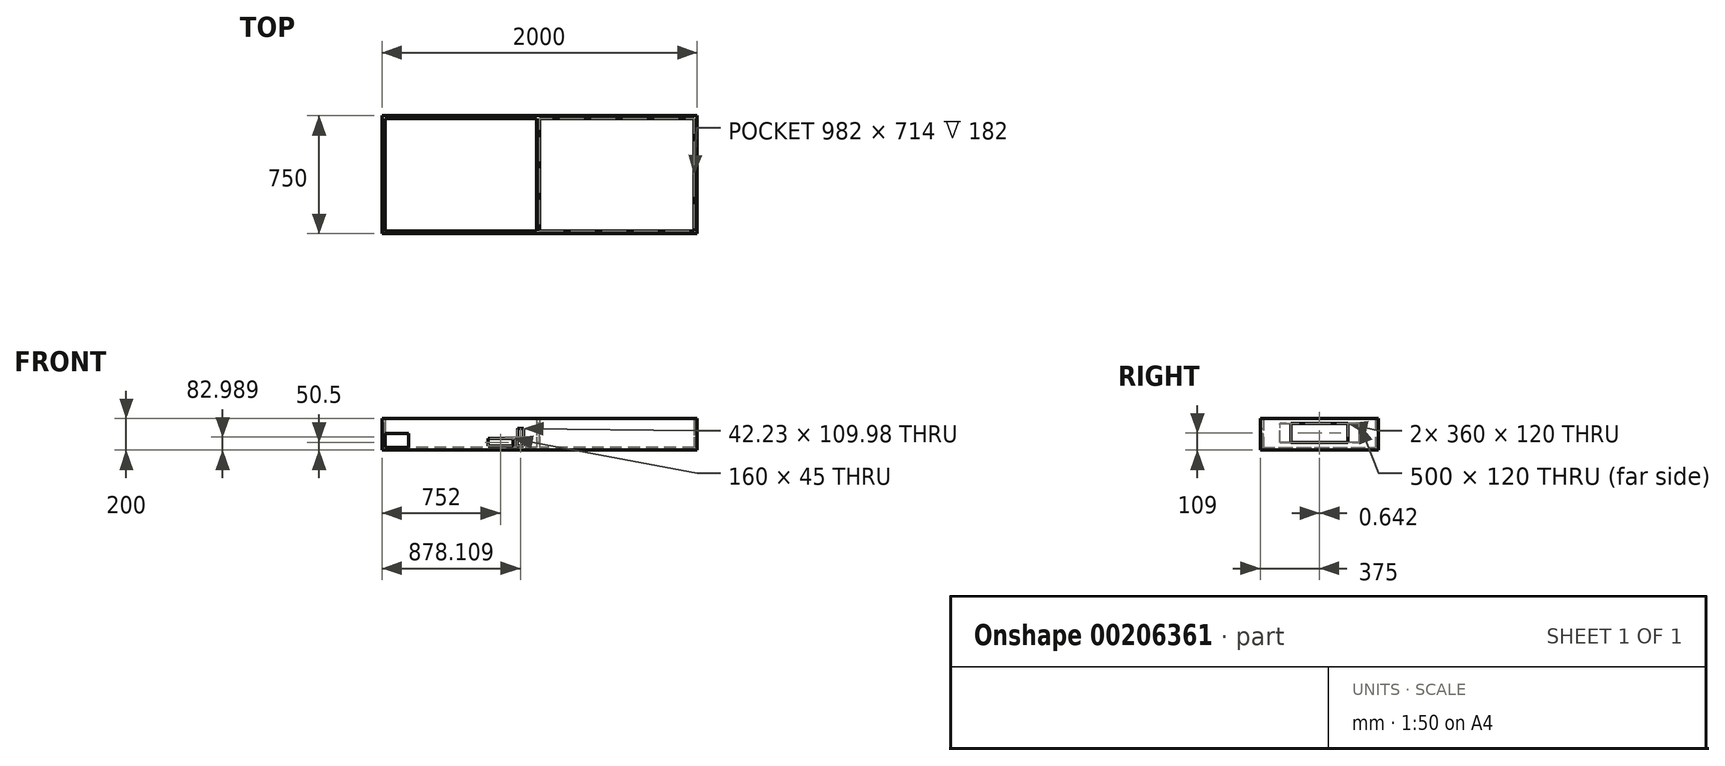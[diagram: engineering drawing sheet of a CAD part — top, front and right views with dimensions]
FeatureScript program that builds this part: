
annotation { "Feature Type Name" : "Feature", "Feature Type Description" : "" }
export const myFeature = defineFeature(function(context is Context, id is Id, definition is map)
    precondition{}
    {
        {
            var Q0;
            Q0=qCreatedBy(makeId("Top.planeOp"),FACE);
            var sketch = newSketch(context, id + "F0", { "sketchPlane" : qUnion([Q0])});
            skLineSegment(sketch, "E0.bottom", {"start": v(1000, -375) * mm, "end": v(-1000, -375) * mm});
            skLineSegment(sketch, "E0.top", {"start": v(1000, 375) * mm, "end": v(-1000, 375) * mm});
            skLineSegment(sketch, "E0.left", {"start": v(1000, -375) * mm, "end": v(1000, 375) * mm});
            skLineSegment(sketch, "E0.right", {"start": v(-1000, -375) * mm, "end": v(-1000, 375) * mm});
            skPoint(sketch, "E0.middle", {"position": v(0, 0) * mm});
            skSolve(sketch);
        }
        {
            var Q0;
            Q0=makeQuery(id+"F0.imprint","IMPRINT",FACE,{"disambiguationData":[TD([[makeQuery(id+"F0.imprint","IMPRINT",EDGE,{"derivedFrom":sQuery(id+"F0.wireOp",EDGE,"E0.bottom")}),-1.0]])]});
            extrude(context, id + "F1", {"entities" : qUnion([Q0]), "depth" : 200 * mm});
        }
        {
            var Q0;
            Q0=makeQuery(id+"F1.opExtrude","CAP_FACE",FACE,{"disambiguationData":[OSD([sQuery(id+"F0.wireOp",EDGE,"E0.bottom"),sQuery(id+"F0.wireOp",EDGE,"E0.top"),sQuery(id+"F0.wireOp",EDGE,"E0.left"),sQuery(id+"F0.wireOp",EDGE,"E0.right")])],"isStart":false});
            shell(context, id + "F2", {"entities" : qUnion([Q0]), "thickness" : 18 * mm});
        }
        {
            var Q0;
            Q0=makeQuery(id+"F2.opShell","OFFSET_FACE",FACE,{"disambiguationData":[OSD([sQuery(id+"F0.wireOp",EDGE,"E0.bottom"),sQuery(id+"F0.wireOp",EDGE,"E0.top"),sQuery(id+"F0.wireOp",EDGE,"E0.left"),sQuery(id+"F0.wireOp",EDGE,"E0.right")])]});
            var sketch = newSketch(context, id + "F3", { "sketchPlane" : qUnion([Q0])});
            skLineSegment(sketch, "E1.bottom", {"start": v(0, 357) * mm, "end": v(-18, 357) * mm});
            skLineSegment(sketch, "E1.top", {"start": v(0, -357) * mm, "end": v(-18, -357) * mm});
            skLineSegment(sketch, "E1.left", {"start": v(0, 357) * mm, "end": v(0, -357) * mm});
            skLineSegment(sketch, "E1.right", {"start": v(-18, 357) * mm, "end": v(-18, -357) * mm});
            skSolve(sketch);
        }
        {
            var Q0;
            Q0=makeQuery(id+"F3.imprint","IMPRINT",FACE,{"disambiguationData":[TD([[makeQuery(id+"F3.imprint","IMPRINT",EDGE,{"derivedFrom":sQuery(id+"F3.wireOp",EDGE,"E1.bottom")}),1.0]])]});
            extrude(context, id + "F4", {"entities" : qUnion([Q0]), "operationType" : NewBodyOperationType.ADD, "depth" : 182 * mm});
        }
        {
            var Q0;
            Q0=makeQuery(id+"F4.opExtrude","SWEPT_FACE",FACE,{"disambiguationData":[OSD([sQuery(id+"F3.wireOp",EDGE,"E1.right")])]});
            var sketch = newSketch(context, id + "F5", { "sketchPlane" : qUnion([Q0])});
            skLineSegment(sketch, "E2", {"start": v(0, 200) * mm, "end": v(0, 169) * mm});
            skLineSegment(sketch, "E3", {"start": v(0, 169) * mm, "end": v(250, 169) * mm});
            skLineSegment(sketch, "E4", {"start": v(250, 169) * mm, "end": v(250, 49) * mm});
            skLineSegment(sketch, "E5", {"start": v(250, 49) * mm, "end": v(-250, 49) * mm});
            skLineSegment(sketch, "E6", {"start": v(-250, 49) * mm, "end": v(-250, 169) * mm});
            skLineSegment(sketch, "E7", {"start": v(-250, 169) * mm, "end": v(0, 169) * mm});
            skSolve(sketch);
        }
        {
            var Q0;
            Q0=makeQuery(id+"F5.imprint","IMPRINT",FACE,{"disambiguationData":[TD([[makeQuery(id+"F5.imprint","IMPRINT",EDGE,{"derivedFrom":sQuery(id+"F5.wireOp",EDGE,"E3")}),-1.0]])]});
            extrude(context, id + "F6", {"entities" : qUnion([Q0]), "operationType" : NewBodyOperationType.REMOVE, "oppositeDirection" : true, "depth" : 25 * mm});
        }
        {
            var Q0;
            {var subQ1=sQuery(id+"F0.wireOp",EDGE,"E0.right");var subQ4=sQuery(id+"F0.wireOp",EDGE,"E0.bottom");Q0=makeQuery(id+"F4.boolean.opBoolean","SPLIT",FACE,{"disambiguationData":[TD([makeQuery(id+"F2.opShell","OFFSET_FACE",FACE,{"disambiguationData":[OSD([subQ1])]})])],"derivedFrom":makeQuery(id+"F2.opShell","OFFSET_FACE",FACE,{"disambiguationData":[OSD([subQ4])]})});}
            var sketch = newSketch(context, id + "F7", { "sketchPlane" : qUnion([Q0])});
            skLineSegment(sketch, "E8.bottom", {"start": v(982, 18) * mm, "end": v(832, 18) * mm});
            skLineSegment(sketch, "E8.top", {"start": v(982, 106.6) * mm, "end": v(832, 106.6) * mm});
            skLineSegment(sketch, "E8.left", {"start": v(982, 18) * mm, "end": v(982, 106.6) * mm});
            skLineSegment(sketch, "E8.right", {"start": v(832, 18) * mm, "end": v(832, 106.6) * mm});
            skLineSegment(sketch, "E9", {"start": v(18, 18) * mm, "end": v(93.34, 18) * mm});
            skLineSegment(sketch, "E10", {"start": v(328, 18) * mm, "end": v(328, 28) * mm});
            skLineSegment(sketch, "E11", {"start": v(328, 28) * mm, "end": v(168, 28) * mm});
            skLineSegment(sketch, "E12", {"start": v(168, 28) * mm, "end": v(168, 18) * mm});
            skLineSegment(sketch, "E13", {"start": v(168, 28) * mm, "end": v(143, 28) * mm});
            skLineSegment(sketch, "E14", {"start": v(143, 28) * mm, "end": v(103, 28) * mm});
            skLineSegment(sketch, "E15", {"start": v(103, 28) * mm, "end": v(18, 28) * mm});
            skLineSegment(sketch, "E16", {"start": v(103, 28) * mm, "end": v(100.78, 137.98) * mm});
            skLineSegment(sketch, "E17", {"start": v(100.78, 137.98) * mm, "end": v(140.78, 137.98) * mm});
            skLineSegment(sketch, "E18", {"start": v(140.78, 137.98) * mm, "end": v(143, 28) * mm});
            skLineSegment(sketch, "E19", {"start": v(168, 28) * mm, "end": v(168, 73) * mm});
            skLineSegment(sketch, "E20", {"start": v(168, 73) * mm, "end": v(328, 73) * mm});
            skLineSegment(sketch, "E21", {"start": v(328, 73) * mm, "end": v(328, 28) * mm});
            skSolve(sketch);
        }
        {
            var Q0;
            Q0 = qSketchRegion(id + "F7", true);
            extrude(context, id + "F8", {"entities" : qUnion([Q0]), "operationType" : NewBodyOperationType.REMOVE, "oppositeDirection" : true, "depth" : 25 * mm});
        }
        {
            var Q0;
            Q0 = qSketchRegion(id + "F7", true);
            extrude(context, id + "F9", {"entities" : qUnion([Q0]), "operationType" : NewBodyOperationType.REMOVE, "oppositeDirection" : true, "depth" : 25 * mm});
        }
        {
            var Q0;
            Q0 = qSketchRegion(id + "F7", true);
            extrude(context, id + "F10", {"entities" : qUnion([Q0]), "operationType" : NewBodyOperationType.REMOVE, "oppositeDirection" : true, "depth" : 25 * mm});
        }
        {
            var Q0;
            Q0=makeQuery(id+"F2.opShell","OFFSET_FACE",FACE,{"disambiguationData":[OSD([sQuery(id+"F0.wireOp",EDGE,"E0.left")])]});
            var sketch = newSketch(context, id + "F11", { "sketchPlane" : qUnion([Q0])});
            skLineSegment(sketch, "E22", {"start": v(-357, 18) * mm, "end": v(0, 18) * mm});
            skLineSegment(sketch, "E23", {"start": v(0, 18) * mm, "end": v(180, 18) * mm});
            skLineSegment(sketch, "E24", {"start": v(180, 18) * mm, "end": v(180, 49) * mm});
            skLineSegment(sketch, "E25", {"start": v(180, 49) * mm, "end": v(180, 169) * mm});
            skLineSegment(sketch, "E26", {"start": v(180, 169) * mm, "end": v(-180, 169) * mm});
            skLineSegment(sketch, "E27", {"start": v(-180, 169) * mm, "end": v(-180, 49) * mm});
            skLineSegment(sketch, "E28", {"start": v(-180, 49) * mm, "end": v(180, 49) * mm});
            skSolve(sketch);
        }
        {
            var Q0;
            Q0=makeQuery(id+"F11.imprint","IMPRINT",FACE,{"disambiguationData":[TD([[makeQuery(id+"F11.imprint","IMPRINT",EDGE,{"derivedFrom":sQuery(id+"F11.wireOp",EDGE,"E25")}),1.0]])]});
            extrude(context, id + "F12", {"entities" : qUnion([Q0]), "operationType" : NewBodyOperationType.ADD, "depth" : 25 * mm});
        }
        {
            var Q0;
            Q0=makeQuery(id+"F12.opExtrude","CAP_FACE",FACE,{"disambiguationData":[OSD([sQuery(id+"F11.wireOp",EDGE,"E25"),sQuery(id+"F11.wireOp",EDGE,"E26"),sQuery(id+"F11.wireOp",EDGE,"E27"),sQuery(id+"F11.wireOp",EDGE,"E28")])],"isStart":false});
            extrude(context, id + "F13", {"entities" : qUnion([Q0]), "operationType" : NewBodyOperationType.REMOVE, "oppositeDirection" : true, "depth" : 25 * mm});
        }
        {
            var Q0;
            Q0=makeQuery(id+"F11.imprint","IMPRINT",FACE,{"disambiguationData":[TD([[makeQuery(id+"F11.imprint","IMPRINT",EDGE,{"derivedFrom":sQuery(id+"F11.wireOp",EDGE,"E25")}),1.0]])]});
            extrude(context, id + "F14", {"entities" : qUnion([Q0]), "operationType" : NewBodyOperationType.REMOVE, "oppositeDirection" : true, "depth" : 25 * mm});
        }
        {
            var Q0;
            Q0=makeQuery(id+"F1.opExtrude","SWEPT_FACE",FACE,{"disambiguationData":[OSD([sQuery(id+"F0.wireOp",EDGE,"E0.right")])]});
            var sketch = newSketch(context, id + "F15", { "sketchPlane" : qUnion([Q0])});
            skLineSegment(sketch, "E29", {"start": v(-180.64, 169.02) * mm, "end": v(179.36, 169.02) * mm});
            skLineSegment(sketch, "E30", {"start": v(179.36, 169.02) * mm, "end": v(179.36, 49.02) * mm});
            skLineSegment(sketch, "E31", {"start": v(179.36, 49.02) * mm, "end": v(-180.64, 49.02) * mm});
            skLineSegment(sketch, "E32", {"start": v(-180.64, 49.02) * mm, "end": v(-180.64, 169.02) * mm});
            skSolve(sketch);
        }
        {
            var Q0;
            Q0=makeQuery(id+"F15.imprint","IMPRINT",FACE,{"disambiguationData":[TD([[makeQuery(id+"F15.imprint","IMPRINT",EDGE,{"derivedFrom":sQuery(id+"F15.wireOp",EDGE,"E29")}),-1.0]])]});
            extrude(context, id + "F16", {"entities" : qUnion([Q0]), "operationType" : NewBodyOperationType.REMOVE, "oppositeDirection" : true, "depth" : 20 * mm});
        }
    });
